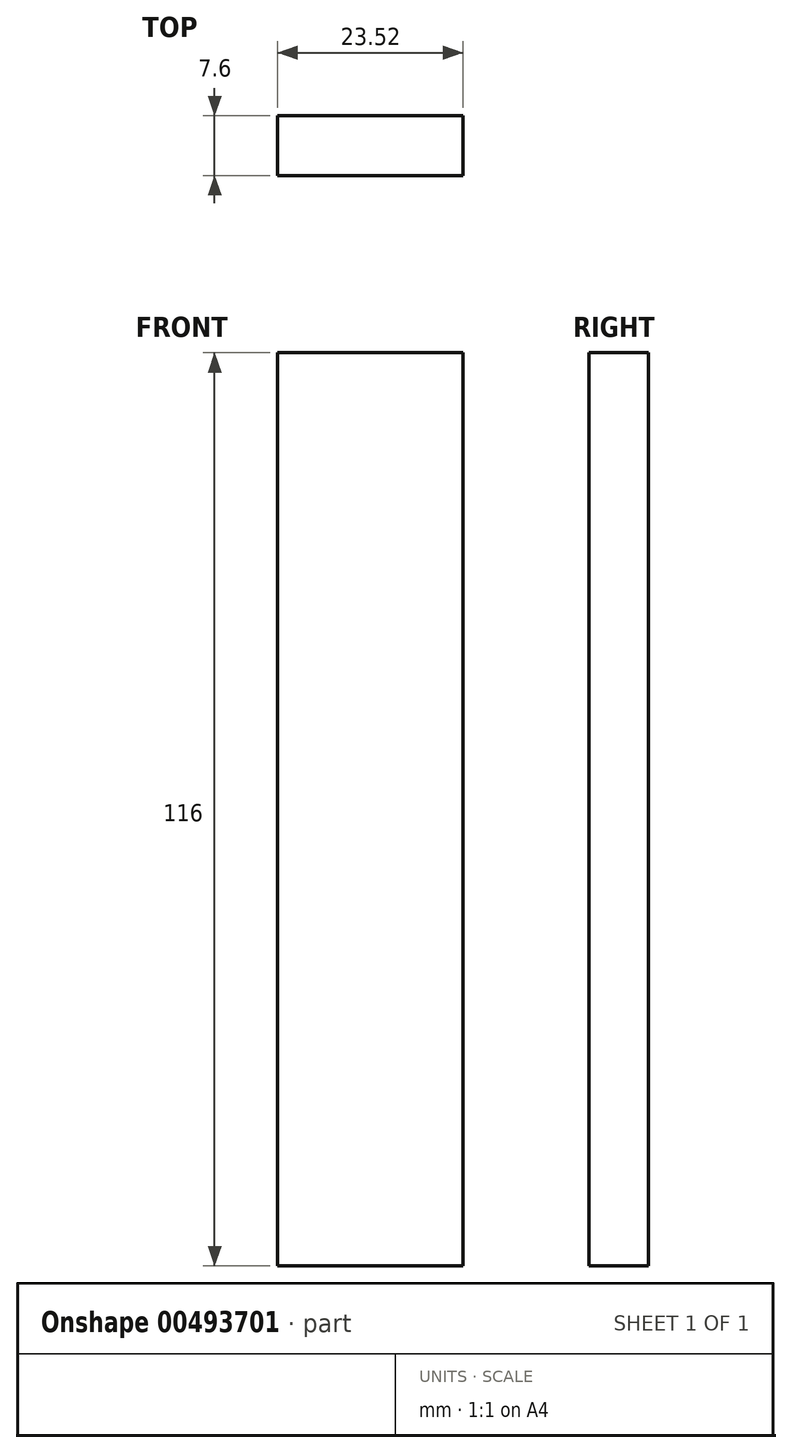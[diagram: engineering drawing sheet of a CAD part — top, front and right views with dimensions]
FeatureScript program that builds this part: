
annotation { "Feature Type Name" : "Feature", "Feature Type Description" : "" }
export const myFeature = defineFeature(function(context is Context, id is Id, definition is map)
    precondition{}
    {
        {
            var Q0;
            Q0=qCreatedBy(makeId("Front.planeOp"),FACE);
            var sketch = newSketch(context, id + "F0", { "sketchPlane" : qUnion([Q0])});
            skLineSegment(sketch, "E0.bottom", {"start": v(-11.76, 58) * mm, "end": v(11.76, 58) * mm});
            skLineSegment(sketch, "E0.top", {"start": v(-11.76, -58) * mm, "end": v(11.76, -58) * mm});
            skLineSegment(sketch, "E0.left", {"start": v(-11.76, 58) * mm, "end": v(-11.76, -58) * mm});
            skLineSegment(sketch, "E0.right", {"start": v(11.76, 58) * mm, "end": v(11.76, -58) * mm});
            skPoint(sketch, "E0.middle", {"position": v(0, 0) * mm});
            skSolve(sketch);
        }
        {
            var Q0;
            Q0=makeQuery(id+"F0.imprint","IMPRINT",FACE,{"disambiguationData":[TD([[makeQuery(id+"F0.imprint","IMPRINT",EDGE,{"derivedFrom":sQuery(id+"F0.wireOp",EDGE,"E0.bottom")}),-1.0]])]});
            extrude(context, id + "F1", {"entities" : qUnion([Q0]), "endBound" : BoundingType.SYMMETRIC, "depth" : 7.6 * mm});
        }
    });
